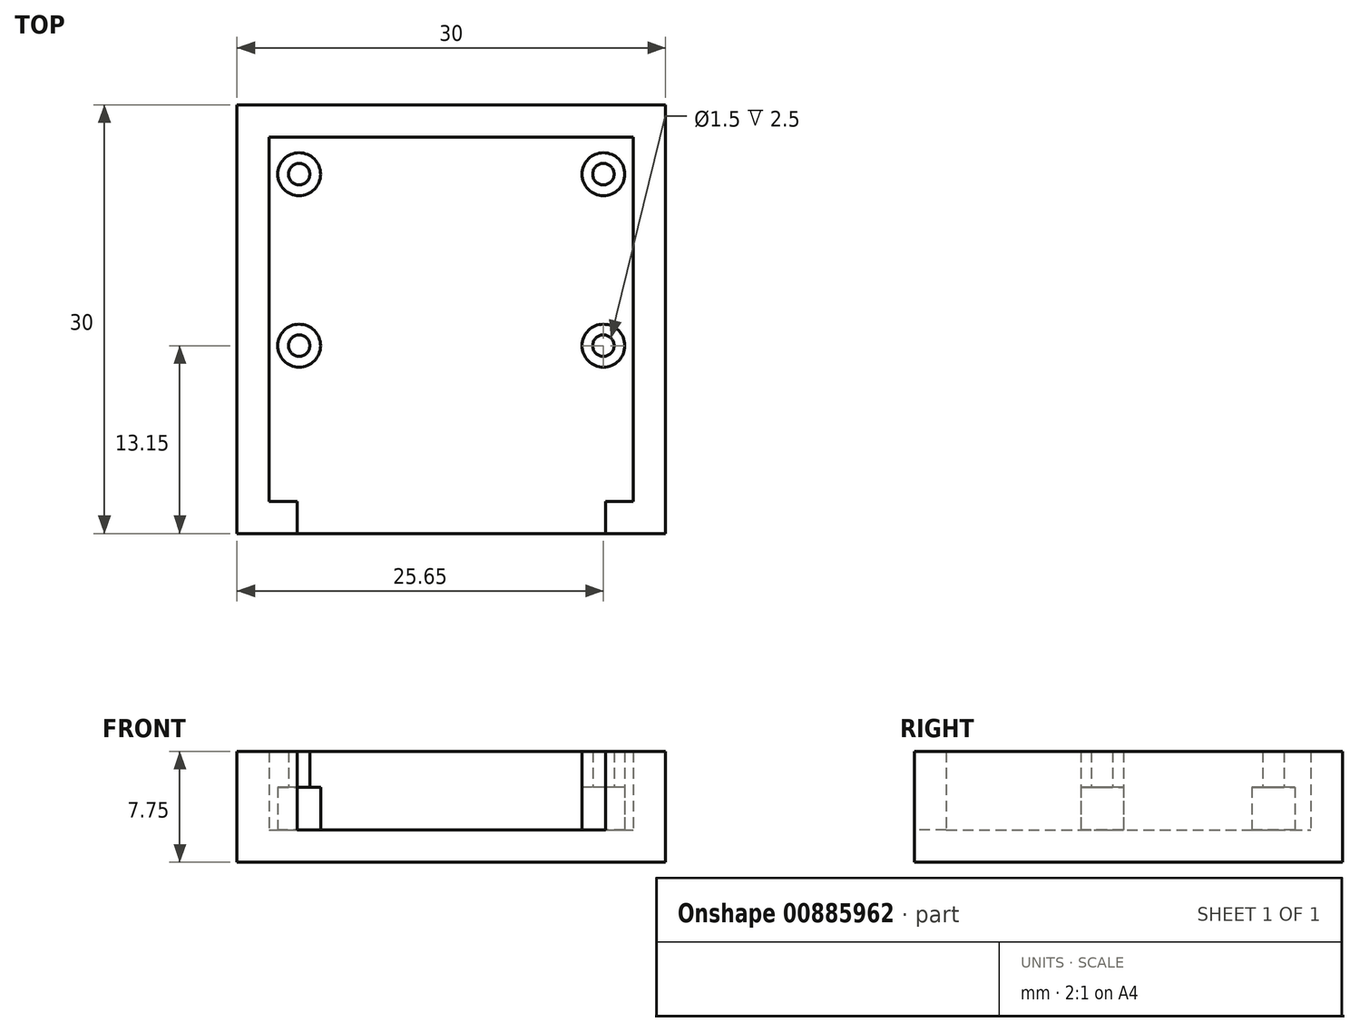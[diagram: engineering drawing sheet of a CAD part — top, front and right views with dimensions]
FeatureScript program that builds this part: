
annotation { "Feature Type Name" : "Feature", "Feature Type Description" : "" }
export const myFeature = defineFeature(function(context is Context, id is Id, definition is map)
    precondition{}
    {
        {
            var Q0;
            Q0=qCreatedBy(makeId("Top.planeOp"),FACE);
            var sketch = newSketch(context, id + "F0", { "sketchPlane" : qUnion([Q0])});
            skLineSegment(sketch, "E0.bottom", {"start": v(0, 0) * mm, "end": v(30, 0) * mm});
            skLineSegment(sketch, "E0.top", {"start": v(0, 30) * mm, "end": v(30, 30) * mm});
            skLineSegment(sketch, "E0.left", {"start": v(0, 0) * mm, "end": v(0, 30) * mm});
            skLineSegment(sketch, "E0.right", {"start": v(30, 0) * mm, "end": v(30, 30) * mm});
            skLineSegment(sketch, "E1.bottom", {"start": v(2.25, 2.25) * mm, "end": v(27.75, 2.25) * mm});
            skLineSegment(sketch, "E1.top", {"start": v(2.25, 27.75) * mm, "end": v(27.75, 27.75) * mm});
            skLineSegment(sketch, "E1.left", {"start": v(2.25, 2.25) * mm, "end": v(2.25, 27.75) * mm});
            skLineSegment(sketch, "E1.right", {"start": v(27.75, 2.25) * mm, "end": v(27.75, 27.75) * mm});
            skLineSegment(sketch, "E2", {"start": v(15, 27.75) * mm, "end": v(15, 30) * mm, "construction": true});
            skLineSegment(sketch, "E3", {"start": v(30, 15) * mm, "end": v(27.75, 15) * mm, "construction": true});
            skLineSegment(sketch, "E4", {"start": v(4.2, 2.25) * mm, "end": v(4.2, 0) * mm});
            skLineSegment(sketch, "E5", {"start": v(25.8, 2.25) * mm, "end": v(25.8, 0) * mm});
            skLineSegment(sketch, "E6.bottom", {"start": v(40.77, 0) * mm, "end": v(70.77, 0) * mm});
            skLineSegment(sketch, "E6.top", {"start": v(40.77, 30) * mm, "end": v(70.77, 30) * mm});
            skLineSegment(sketch, "E6.left", {"start": v(40.77, 0) * mm, "end": v(40.77, 30) * mm});
            skLineSegment(sketch, "E6.right", {"start": v(70.77, 0) * mm, "end": v(70.77, 30) * mm});
            skLineSegment(sketch, "E7.bottom", {"start": v(42.64, 28.25) * mm, "end": v(69.53, 28.25) * mm});
            skLineSegment(sketch, "E7.top", {"start": v(42.64, 2.32) * mm, "end": v(69.53, 2.32) * mm});
            skLineSegment(sketch, "E7.left", {"start": v(42.64, 28.25) * mm, "end": v(42.64, 2.32) * mm});
            skLineSegment(sketch, "E7.right", {"start": v(69.53, 28.25) * mm, "end": v(69.53, 2.32) * mm});
            skSolve(sketch);
        }
        {
            var Q0;
            Q0=makeQuery(id+"F0.imprint","IMPRINT",FACE,{"disambiguationData":[TD([[makeQuery(id+"F0.imprint","IMPRINT",EDGE,{"derivedFrom":sQuery(id+"F0.wireOp",EDGE,"E0.top")}),-1.0]])]});
            extrude(context, id + "F1", {"entities" : qUnion([Q0]), "depth" : 5.5 * mm, "offsetDistance" : 25 * mm});
        }
        {
            var Q0;
            Q0=makeQuery(id+"F0.imprint","IMPRINT",FACE,{"disambiguationData":[TD([[makeQuery(id+"F0.imprint","IMPRINT",EDGE,{"derivedFrom":sQuery(id+"F0.wireOp",EDGE,"E1.top")}),-1.0]])]});
            var Q1;
            Q1=makeQuery(id+"F0.imprint","IMPRINT",FACE,{"disambiguationData":[TD([[makeQuery(id+"F0.imprint","IMPRINT",EDGE,{"derivedFrom":sQuery(id+"F0.wireOp",EDGE,"E0.top")}),-1.0]])]});
            var Q2;
            {var subQ0=sQuery(id+"F0.wireOp",EDGE,"E4");Q2=makeQuery(id+"F0.imprint","IMPRINT",FACE,{"disambiguationData":[TD([[makeQuery(id+"F0.imprint","IMPRINT",EDGE,{"derivedFrom":subQ0}),1.0]])]});}
            extrude(context, id + "F2", {"entities" : qUnion([Q0, Q1, Q2]), "operationType" : NewBodyOperationType.ADD, "oppositeDirection" : true, "depth" : 2.25 * mm, "offsetDistance" : 25 * mm});
        }
        {
            var Q0;
            Q0=makeQuery(id+"F0.imprint","IMPRINT",FACE,{"disambiguationData":[TD([[makeQuery(id+"F0.imprint","IMPRINT",EDGE,{"derivedFrom":sQuery(id+"F0.wireOp",EDGE,"E1.top")}),-1.0]])]});
            var sketch = newSketch(context, id + "F3", { "sketchPlane" : qUnion([Q0])});
            skLineSegment(sketch, "E8.bottom", {"start": v(2.5, 27) * mm, "end": v(27.5, 27) * mm});
            skLineSegment(sketch, "E8.top", {"start": v(2.5, 3) * mm, "end": v(27.5, 3) * mm});
            skLineSegment(sketch, "E8.left", {"start": v(2.5, 27) * mm, "end": v(2.5, 3) * mm});
            skLineSegment(sketch, "E8.right", {"start": v(27.5, 27) * mm, "end": v(27.5, 3) * mm});
            skLineSegment(sketch, "E9", {"start": v(15, 27) * mm, "end": v(15, 27.75) * mm, "construction": true});
            skLineSegment(sketch, "E10", {"start": v(2.5, 15) * mm, "end": v(2.25, 15) * mm, "construction": true});
            skCircle(sketch, "E11", {"center": v(25.65, 25.15) * mm, "radius": 0.75 * mm});
            skCircle(sketch, "E12", {"center": v(4.35, 25.15) * mm, "radius": 0.75 * mm});
            skCircle(sketch, "E13", {"center": v(25.65, 13.15) * mm, "radius": 0.75 * mm});
            skLineSegment(sketch, "E14", {"start": v(25.65, 13.15) * mm, "end": v(25.65, 25.15) * mm, "construction": true});
            skLineSegment(sketch, "E15", {"start": v(25.65, 13.15) * mm, "end": v(4.35, 13.15) * mm, "construction": true});
            skLineSegment(sketch, "E16", {"start": v(4.35, 13.15) * mm, "end": v(4.35, 25.15) * mm, "construction": true});
            skCircle(sketch, "E17", {"center": v(4.35, 13.15) * mm, "radius": 0.75 * mm});
            skCircle(sketch, "E18", {"center": v(4.35, 13.15) * mm, "radius": 1.5 * mm});
            skCircle(sketch, "E19", {"center": v(4.35, 25.15) * mm, "radius": 1.5 * mm});
            skCircle(sketch, "E20", {"center": v(25.65, 25.15) * mm, "radius": 1.5 * mm});
            skCircle(sketch, "E21", {"center": v(25.65, 13.15) * mm, "radius": 1.5 * mm});
            skSolve(sketch);
        }
        {
            var Q0;
            Q0=makeQuery(id+"F3.imprint","IMPRINT",FACE,{"disambiguationData":[TD([[makeQuery(id+"F3.imprint","IMPRINT",EDGE,{"derivedFrom":sQuery(id+"F3.wireOp",EDGE,"E11")}),-1.0]])]});
            var Q1;
            Q1=makeQuery(id+"F3.imprint","IMPRINT",FACE,{"disambiguationData":[TD([[makeQuery(id+"F3.imprint","IMPRINT",EDGE,{"derivedFrom":sQuery(id+"F3.wireOp",EDGE,"E13")}),1.0]])]});
            var Q2;
            Q2=makeQuery(id+"F3.imprint","IMPRINT",FACE,{"disambiguationData":[TD([[makeQuery(id+"F3.imprint","IMPRINT",EDGE,{"derivedFrom":sQuery(id+"F3.wireOp",EDGE,"E12")}),-1.0]])]});
            var Q3;
            Q3=makeQuery(id+"F3.imprint","IMPRINT",FACE,{"disambiguationData":[TD([[makeQuery(id+"F3.imprint","IMPRINT",EDGE,{"derivedFrom":sQuery(id+"F3.wireOp",EDGE,"E17")}),-1.0]])]});
            extrude(context, id + "F4", {"entities" : qUnion([Q0, Q1, Q2, Q3]), "operationType" : NewBodyOperationType.ADD, "depth" : 3 * mm, "offsetDistance" : 25 * mm});
        }
        {
            var Q0;
            Q0=makeQuery(id+"F3.imprint","IMPRINT",FACE,{"disambiguationData":[TD([[makeQuery(id+"F3.imprint","IMPRINT",EDGE,{"derivedFrom":sQuery(id+"F3.wireOp",EDGE,"E12")}),1.0]])]});
            var Q1;
            Q1=makeQuery(id+"F3.imprint","IMPRINT",FACE,{"disambiguationData":[TD([[makeQuery(id+"F3.imprint","IMPRINT",EDGE,{"derivedFrom":sQuery(id+"F3.wireOp",EDGE,"E11")}),1.0]])]});
            var Q2;
            Q2=makeQuery(id+"F3.imprint","IMPRINT",FACE,{"disambiguationData":[TD([[makeQuery(id+"F3.imprint","IMPRINT",EDGE,{"derivedFrom":sQuery(id+"F3.wireOp",EDGE,"E13")}),-1.0]])]});
            var Q3;
            Q3=makeQuery(id+"F3.imprint","IMPRINT",FACE,{"disambiguationData":[TD([[makeQuery(id+"F3.imprint","IMPRINT",EDGE,{"derivedFrom":sQuery(id+"F3.wireOp",EDGE,"E17")}),1.0]])]});
            extrude(context, id + "F5", {"entities" : qUnion([Q0, Q1, Q2, Q3]), "operationType" : NewBodyOperationType.ADD, "depth" : 5.5 * mm, "offsetDistance" : 25 * mm});
        }
    });
